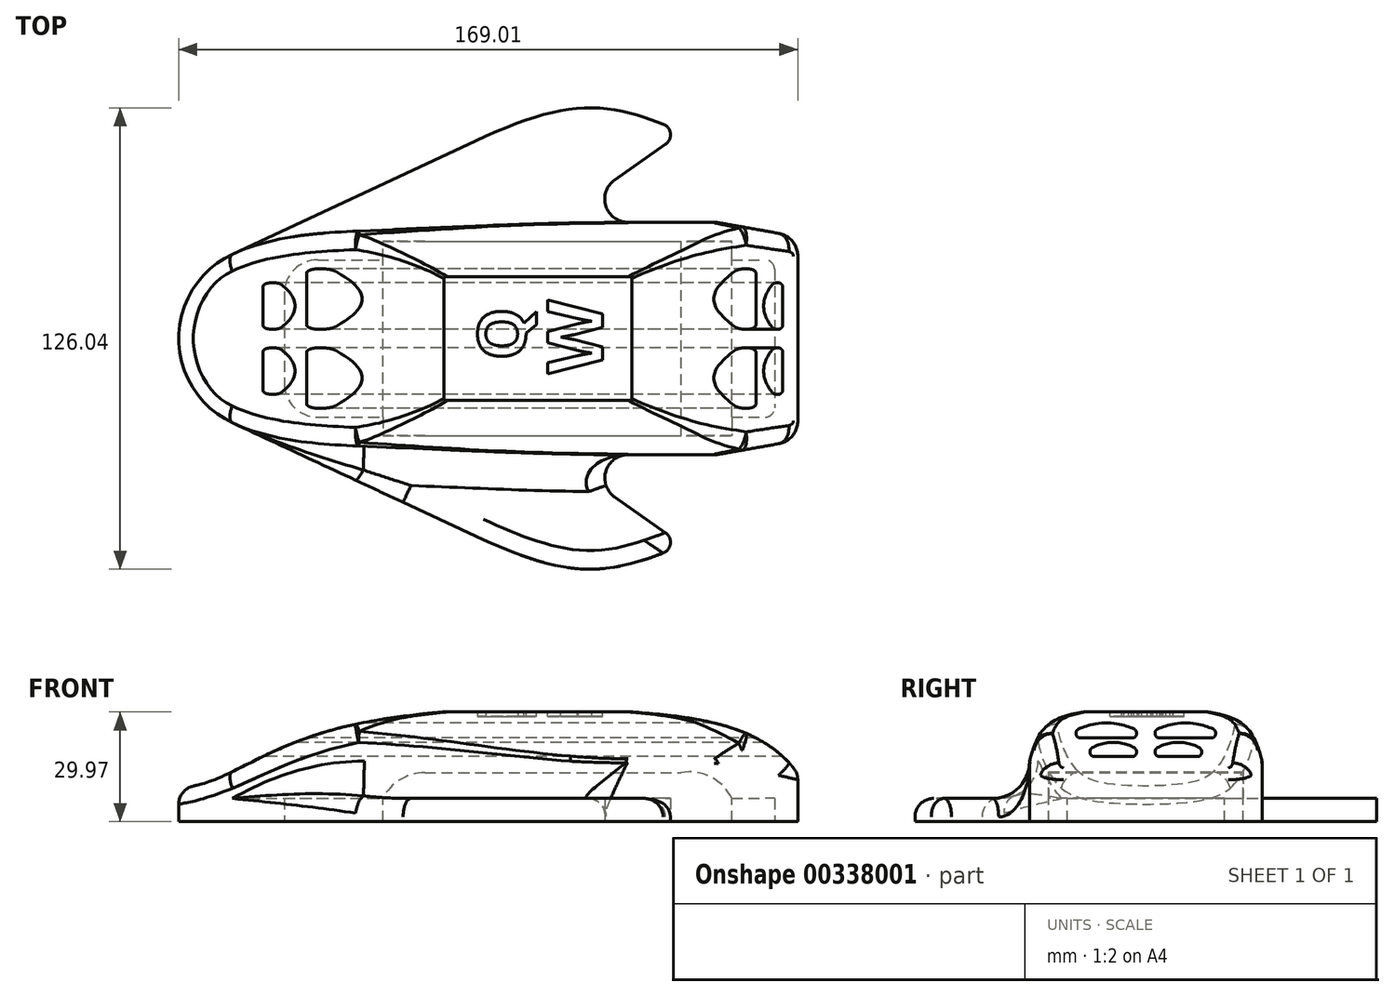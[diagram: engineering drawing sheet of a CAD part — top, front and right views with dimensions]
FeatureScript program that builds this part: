
annotation { "Feature Type Name" : "Feature", "Feature Type Description" : "" }
export const myFeature = defineFeature(function(context is Context, id is Id, definition is map)
    precondition{}
    {
        {
            var Q0;
            Q0=qCreatedBy(makeId("Top.planeOp"),FACE);
            var sketch = newSketch(context, id + "F0", { "sketchPlane" : qUnion([Q0])});
            skLineSegment(sketch, "E0", {"start": v(-59.71, 0) * mm, "end": v(137.74, 0) * mm, "construction": true});
            skLineSegment(sketch, "E1", {"start": v(0, 0) * mm, "end": v(0, 12.32) * mm});
            skLineSegment(sketch, "E2", {"start": v(9.14, 21.46) * mm, "end": v(131.32, 21.46) * mm});
            skLineSegment(sketch, "E3", {"start": v(133.86, 18.92) * mm, "end": v(133.86, 0) * mm});
            skPoint(sketch, "E4.visualSharp", {"position": v(0, 21.46) * mm});
            skArc(sketch, "E4.filletArc", {"start": v(9.14, 21.46) * mm, "mid": v(2.68, 18.78) * mm, "end": v(0, 12.32) * mm});
            skPoint(sketch, "E5.visualSharp", {"position": v(133.86, 21.46) * mm});
            skArc(sketch, "E5.filletArc", {"start": v(133.86, 18.92) * mm, "mid": v(133.11, 20.72) * mm, "end": v(131.32, 21.46) * mm});
            skLineSegment(sketch, "E6", {"start": v(-14.13, 23.02) * mm, "end": v(52.25, 53.98) * mm});
            skLineSegment(sketch, "E7", {"start": v(104.12, 53.03) * mm, "end": v(90.22, 43.3) * mm});
            skLineSegment(sketch, "E8", {"start": v(93.86, 31.75) * mm, "end": v(117.43, 31.75) * mm});
            skLineSegment(sketch, "E9", {"start": v(140.2, 22.5) * mm, "end": v(140.2, 0) * mm});
            skPoint(sketch, "E10.visualSharp", {"position": v(73.72, 31.75) * mm});
            skArc(sketch, "E10.filletArc", {"start": v(90.22, 43.3) * mm, "mid": v(87.8, 36.2) * mm, "end": v(93.86, 31.75) * mm});
            skLineSegment(sketch, "E11", {"start": v(118.53, 31.65) * mm, "end": v(134.96, 28.76) * mm});
            skPoint(sketch, "E12.visualSharp", {"position": v(117.98, 31.75) * mm});
            skArc(sketch, "E12.filletArc", {"start": v(118.53, 31.65) * mm, "mid": v(117.98, 31.73) * mm, "end": v(117.43, 31.75) * mm});
            skPoint(sketch, "E13.visualSharp", {"position": v(140.2, 27.83) * mm});
            skArc(sketch, "E13.filletArc", {"start": v(140.2, 22.5) * mm, "mid": v(138.72, 26.58) * mm, "end": v(134.96, 28.76) * mm});
            skArc(sketch, "E14.MirrorCS", {"start": v(118.53, -31.65) * mm, "mid": v(117.98, -31.73) * mm, "end": v(117.43, -31.75) * mm});
            skArc(sketch, "E15.MirrorCS", {"start": v(133.86, -18.92) * mm, "mid": v(133.11, -20.72) * mm, "end": v(131.32, -21.46) * mm});
            skArc(sketch, "E16.MirrorCS", {"start": v(140.2, -22.5) * mm, "mid": v(138.72, -26.58) * mm, "end": v(134.96, -28.76) * mm});
            skPoint(sketch, "E17.MirrorP", {"position": v(140.2, -27.83) * mm});
            skPoint(sketch, "E18.MirrorP", {"position": v(73.72, -31.75) * mm});
            skPoint(sketch, "E19.MirrorP", {"position": v(117.98, -31.75) * mm});
            skLineSegment(sketch, "E20.MirrorCS", {"start": v(0, 0) * mm, "end": v(0, -12.32) * mm});
            skLineSegment(sketch, "E21.MirrorCS", {"start": v(140.2, -22.5) * mm, "end": v(140.2, 0) * mm});
            skLineSegment(sketch, "E22.MirrorCS", {"start": v(133.86, -18.92) * mm, "end": v(133.86, 0) * mm});
            skPoint(sketch, "E23.MirrorP", {"position": v(0, -21.46) * mm});
            skPoint(sketch, "E24.MirrorP", {"position": v(133.86, -21.46) * mm});
            skLineSegment(sketch, "E25.MirrorCS", {"start": v(118.53, -31.65) * mm, "end": v(134.96, -28.76) * mm});
            skLineSegment(sketch, "E26.MirrorCS", {"start": v(9.14, -21.46) * mm, "end": v(131.32, -21.46) * mm});
            skArc(sketch, "E27.MirrorCS", {"start": v(9.14, -21.46) * mm, "mid": v(2.68, -18.78) * mm, "end": v(0, -12.32) * mm});
            skPoint(sketch, "E28.visualSharp", {"position": v(-63.5, 0) * mm});
            skArc(sketch, "E28.filletArc", {"start": v(-14.13, 23.02) * mm, "mid": v(-24.82, 13.65) * mm, "end": v(-28.8, 0) * mm});
            skFitSpline(sketch, "E29", {"points": [v(106.45, 57.34) * mm, v(86.26, 62.92) * mm, v(52.25, 53.98) * mm], "startDerivative": vector(-36.27, 15.72) * mm, "endDerivative": vector(-75.5, -35.21) * mm});
            skArc(sketch, "E30.filletArc", {"start": v(104.12, 53.03) * mm, "mid": v(105.45, 56) * mm, "end": v(103.47, 58.58) * mm});
            skFitSpline(sketch, "E31.MirrorCS", {"points": [v(106.45, -57.34) * mm, v(86.26, -62.92) * mm, v(52.25, -53.98) * mm], "startDerivative": vector(-36.27, -15.72) * mm, "endDerivative": vector(-75.5, 35.21) * mm});
            skLineSegment(sketch, "E32.MirrorCS", {"start": v(104.12, -53.03) * mm, "end": v(90.22, -43.3) * mm});
            skArc(sketch, "E33.MirrorCS", {"start": v(90.22, -43.3) * mm, "mid": v(87.8, -36.2) * mm, "end": v(93.86, -31.75) * mm});
            skArc(sketch, "E34.MirrorCS", {"start": v(104.12, -53.03) * mm, "mid": v(105.45, -56) * mm, "end": v(103.47, -58.58) * mm});
            skLineSegment(sketch, "E35.MirrorCS", {"start": v(93.86, -31.75) * mm, "end": v(117.43, -31.75) * mm});
            skLineSegment(sketch, "E36.MirrorCS", {"start": v(-14.13, -23.02) * mm, "end": v(52.25, -53.98) * mm});
            skArc(sketch, "E37.MirrorCS", {"start": v(-14.13, -23.02) * mm, "mid": v(-24.82, -13.65) * mm, "end": v(-28.8, 0) * mm});
            skSolve(sketch);
        }
        {
            var Q0;
            Q0 = qSketchRegion(id + "F0", true);
            extrude(context, id + "F1", {"entities" : qUnion([Q0]), "depth" : 6.35 * mm});
        }
        {
            var Q0;
            Q0=makeQuery(id+"F1.opExtrude","CAP_FACE",FACE,{"disambiguationData":[OSD([sQuery(id+"F0.wireOp",EDGE,"E1"),sQuery(id+"F0.wireOp",EDGE,"E2"),sQuery(id+"F0.wireOp",EDGE,"E3"),sQuery(id+"F0.wireOp",EDGE,"E4.filletArc"),sQuery(id+"F0.wireOp",EDGE,"E5.filletArc"),sQuery(id+"F0.wireOp",EDGE,"E6"),sQuery(id+"F0.wireOp",EDGE,"E7"),sQuery(id+"F0.wireOp",EDGE,"E8"),sQuery(id+"F0.wireOp",EDGE,"E9"),sQuery(id+"F0.wireOp",EDGE,"E10.filletArc"),sQuery(id+"F0.wireOp",EDGE,"E11"),sQuery(id+"F0.wireOp",EDGE,"E12.filletArc"),sQuery(id+"F0.wireOp",EDGE,"E13.filletArc"),sQuery(id+"F0.wireOp",EDGE,"E14.MirrorCS"),sQuery(id+"F0.wireOp",EDGE,"E15.MirrorCS"),sQuery(id+"F0.wireOp",EDGE,"E16.MirrorCS"),sQuery(id+"F0.wireOp",EDGE,"E20.MirrorCS"),sQuery(id+"F0.wireOp",EDGE,"E21.MirrorCS"),sQuery(id+"F0.wireOp",EDGE,"E22.MirrorCS"),sQuery(id+"F0.wireOp",EDGE,"E25.MirrorCS"),sQuery(id+"F0.wireOp",EDGE,"E26.MirrorCS"),sQuery(id+"F0.wireOp",EDGE,"E27.MirrorCS"),sQuery(id+"F0.wireOp",EDGE,"E28.filletArc"),sQuery(id+"F0.wireOp",EDGE,"E29"),sQuery(id+"F0.wireOp",EDGE,"E30.filletArc"),sQuery(id+"F0.wireOp",EDGE,"E31.MirrorCS"),sQuery(id+"F0.wireOp",EDGE,"E32.MirrorCS"),sQuery(id+"F0.wireOp",EDGE,"E33.MirrorCS"),sQuery(id+"F0.wireOp",EDGE,"E34.MirrorCS"),sQuery(id+"F0.wireOp",EDGE,"E35.MirrorCS"),sQuery(id+"F0.wireOp",EDGE,"E36.MirrorCS"),sQuery(id+"F0.wireOp",EDGE,"E37.MirrorCS")])],"isStart":false});
            var sketch = newSketch(context, id + "F2", { "sketchPlane" : qUnion([Q0])});
            skLineSegment(sketch, "E38.bottom", {"start": v(99.31, 21.46) * mm, "end": v(122.17, 21.46) * mm});
            skLineSegment(sketch, "E38.top", {"start": v(99.31, 26.54) * mm, "end": v(122.17, 26.54) * mm});
            skLineSegment(sketch, "E38.left", {"start": v(99.31, 21.46) * mm, "end": v(99.31, 26.54) * mm});
            skLineSegment(sketch, "E38.right", {"start": v(122.17, 21.46) * mm, "end": v(122.17, 26.54) * mm});
            skLineSegment(sketch, "E39", {"start": v(0, 0) * mm, "end": v(133.86, 0) * mm, "construction": true});
            skLineSegment(sketch, "E40.MirrorCS", {"start": v(122.17, -21.46) * mm, "end": v(122.17, -26.54) * mm});
            skLineSegment(sketch, "E41.MirrorCS", {"start": v(99.31, -21.46) * mm, "end": v(99.31, -26.54) * mm});
            skLineSegment(sketch, "E42.MirrorCS", {"start": v(99.31, -21.46) * mm, "end": v(122.17, -21.46) * mm});
            skLineSegment(sketch, "E43.MirrorCS", {"start": v(99.31, -26.54) * mm, "end": v(122.17, -26.54) * mm});
            skLineSegment(sketch, "E44.bottom", {"start": v(26.92, 21.46) * mm, "end": v(49.78, 21.46) * mm});
            skLineSegment(sketch, "E44.top", {"start": v(26.92, 26.54) * mm, "end": v(49.78, 26.54) * mm});
            skLineSegment(sketch, "E44.left", {"start": v(26.92, 21.46) * mm, "end": v(26.92, 26.54) * mm});
            skLineSegment(sketch, "E44.right", {"start": v(49.78, 21.46) * mm, "end": v(49.78, 26.54) * mm});
            skLineSegment(sketch, "E45.MirrorCS", {"start": v(26.92, -26.54) * mm, "end": v(49.78, -26.54) * mm});
            skLineSegment(sketch, "E46.MirrorCS", {"start": v(26.92, -21.46) * mm, "end": v(49.78, -21.46) * mm});
            skLineSegment(sketch, "E47.MirrorCS", {"start": v(49.78, -21.46) * mm, "end": v(49.78, -26.54) * mm});
            skLineSegment(sketch, "E48.MirrorCS", {"start": v(26.92, -21.46) * mm, "end": v(26.92, -26.54) * mm});
            skSolve(sketch);
        }
        {
            var Q0;
            Q0 = qSketchRegion(id + "F2", true);
            extrude(context, id + "F3", {"entities" : qUnion([Q0]), "operationType" : NewBodyOperationType.REMOVE, "endBound" : BoundingType.THROUGH_ALL, "oppositeDirection" : true, "depth" : 25.4 * mm});
        }
        {
            var Q0;
            Q0=makeQuery(id+"F1.opExtrude","CAP_FACE",FACE,{"disambiguationData":[OSD([sQuery(id+"F0.wireOp",EDGE,"E1"),sQuery(id+"F0.wireOp",EDGE,"E2"),sQuery(id+"F0.wireOp",EDGE,"E3"),sQuery(id+"F0.wireOp",EDGE,"E4.filletArc"),sQuery(id+"F0.wireOp",EDGE,"E5.filletArc"),sQuery(id+"F0.wireOp",EDGE,"E6"),sQuery(id+"F0.wireOp",EDGE,"E7"),sQuery(id+"F0.wireOp",EDGE,"E8"),sQuery(id+"F0.wireOp",EDGE,"E9"),sQuery(id+"F0.wireOp",EDGE,"E10.filletArc"),sQuery(id+"F0.wireOp",EDGE,"E11"),sQuery(id+"F0.wireOp",EDGE,"E12.filletArc"),sQuery(id+"F0.wireOp",EDGE,"E13.filletArc"),sQuery(id+"F0.wireOp",EDGE,"E14.MirrorCS"),sQuery(id+"F0.wireOp",EDGE,"E15.MirrorCS"),sQuery(id+"F0.wireOp",EDGE,"E16.MirrorCS"),sQuery(id+"F0.wireOp",EDGE,"E20.MirrorCS"),sQuery(id+"F0.wireOp",EDGE,"E21.MirrorCS"),sQuery(id+"F0.wireOp",EDGE,"E22.MirrorCS"),sQuery(id+"F0.wireOp",EDGE,"E25.MirrorCS"),sQuery(id+"F0.wireOp",EDGE,"E26.MirrorCS"),sQuery(id+"F0.wireOp",EDGE,"E27.MirrorCS"),sQuery(id+"F0.wireOp",EDGE,"E28.filletArc"),sQuery(id+"F0.wireOp",EDGE,"E29"),sQuery(id+"F0.wireOp",EDGE,"E30.filletArc"),sQuery(id+"F0.wireOp",EDGE,"E31.MirrorCS"),sQuery(id+"F0.wireOp",EDGE,"E32.MirrorCS"),sQuery(id+"F0.wireOp",EDGE,"E33.MirrorCS"),sQuery(id+"F0.wireOp",EDGE,"E34.MirrorCS"),sQuery(id+"F0.wireOp",EDGE,"E35.MirrorCS"),sQuery(id+"F0.wireOp",EDGE,"E36.MirrorCS"),sQuery(id+"F0.wireOp",EDGE,"E37.MirrorCS")])],"isStart":false});
            var sketch = newSketch(context, id + "F4", { "sketchPlane" : qUnion([Q0])});
            skLineSegment(sketch, "E49.0", {"start": v(93.86, 31.75) * mm, "end": v(117.43, 31.75) * mm});
            skLineSegment(sketch, "E50.0", {"start": v(93.86, -31.75) * mm, "end": v(117.43, -31.75) * mm});
            skArc(sketch, "E51.0", {"start": v(-14.13, 23.02) * mm, "mid": v(-28.8, 0) * mm, "end": v(-14.13, -23.02) * mm});
            skFitSpline(sketch, "E52", {"points": [v(-14.13, -23.02) * mm, v(27.68, -29.68) * mm, v(93.86, -31.75) * mm], "startDerivative": vector(81.8, -38.14) * mm, "endDerivative": vector(126.05, 0) * mm});
            skLineSegment(sketch, "E53.0", {"start": v(118.53, -31.65) * mm, "end": v(134.96, -28.76) * mm});
            skArc(sketch, "E54.0", {"start": v(140.2, -22.5) * mm, "mid": v(138.72, -26.58) * mm, "end": v(134.96, -28.76) * mm});
            skLineSegment(sketch, "E55.0", {"start": v(140.2, -22.5) * mm, "end": v(140.2, 22.5) * mm});
            skPoint(sketch, "E56.0", {"position": v(138.72, 26.58) * mm});
            skArc(sketch, "E57.0", {"start": v(140.2, 22.5) * mm, "mid": v(138.72, 26.58) * mm, "end": v(134.96, 28.76) * mm});
            skLineSegment(sketch, "E58.0", {"start": v(118.53, 31.65) * mm, "end": v(134.96, 28.76) * mm});
            skArc(sketch, "E59.0", {"start": v(118.53, 31.65) * mm, "mid": v(117.98, 31.73) * mm, "end": v(117.43, 31.75) * mm});
            skArc(sketch, "E60.0", {"start": v(118.53, -31.65) * mm, "mid": v(117.98, -31.73) * mm, "end": v(117.43, -31.75) * mm});
            skLineSegment(sketch, "E61", {"start": v(-36.22, 0) * mm, "end": v(156.3, 0) * mm, "construction": true});
            skPoint(sketch, "E61.endSnap0", {"position": v(133.86, 0) * mm});
            skFitSpline(sketch, "E62.MirrorCS", {"points": [v(-14.13, 23.02) * mm, v(27.68, 29.68) * mm, v(93.86, 31.75) * mm], "startDerivative": vector(81.8, 38.14) * mm, "endDerivative": vector(126.05, 0) * mm});
            skSolve(sketch);
        }
        {
            var Q0;
            Q0 = qSketchRegion(id + "F4", true);
            extrude(context, id + "F5", {"entities" : qUnion([Q0]), "operationType" : NewBodyOperationType.ADD, "depth" : 25.4 * mm});
        }
        {
            var Q0;
            Q0=qCreatedBy(makeId("Front.planeOp"),FACE);
            var sketch = newSketch(context, id + "F6", { "sketchPlane" : qUnion([Q0])});
            skFitSpline(sketch, "E63", {"points": [v(-34.74, 3.67) * mm, v(-21.98, 10.44) * mm, v(10.7, 24.38) * mm, v(96.52, 29.85) * mm, v(142.12, 10.31) * mm, v(144.33, 8.88) * mm], "startDerivative": vector(76.62, 125.54) * mm, "endDerivative": vector(-72.53, 307.03) * mm});
            skLineSegment(sketch, "E64", {"start": v(-34.74, 3.67) * mm, "end": v(-35.8, 38.7) * mm});
            skLineSegment(sketch, "E65", {"start": v(-35.8, 38.7) * mm, "end": v(149.91, 37.4) * mm});
            skLineSegment(sketch, "E66", {"start": v(149.91, 37.4) * mm, "end": v(144.33, 8.88) * mm});
            skSolve(sketch);
        }
        {
            var Q0;
            Q0 = qSketchRegion(id + "F6", true);
            extrude(context, id + "F7", {"entities" : qUnion([Q0]), "operationType" : NewBodyOperationType.REMOVE, "endBound" : BoundingType.THROUGH_ALL, "oppositeDirection" : true, "depth" : 25.4 * mm, "hasSecondDirection" : true, "secondDirectionBound" : SecondDirectionBoundingType.THROUGH_ALL, "secondDirectionOppositeDirection" : false, "secondDirectionDepth" : 25.4 * mm});
        }
        {
            var Q0;
            Q0=qCreatedBy(makeId("Right.planeOp"),FACE);
            var sketch = newSketch(context, id + "F8", { "sketchPlane" : qUnion([Q0])});
            skLineSegment(sketch, "E67", {"start": v(0, 35.48) * mm, "end": v(0, -4.46) * mm, "construction": true});
            skFitSpline(sketch, "E68", {"points": [v(-32.03, 15.47) * mm, v(-26.07, 26.9) * mm, v(0, 30.75) * mm], "startDerivative": vector(8.35, 32.15) * mm, "endDerivative": vector(53.08, 0.27) * mm});
            skLineSegment(sketch, "E69", {"start": v(0, 30.75) * mm, "end": v(0, 38.5) * mm});
            skLineSegment(sketch, "E70", {"start": v(0, 38.5) * mm, "end": v(-36.93, 37.2) * mm});
            skLineSegment(sketch, "E71", {"start": v(-36.93, 37.2) * mm, "end": v(-32.03, 15.47) * mm});
            skLineSegment(sketch, "E72.MirrorCS", {"start": v(0, 38.5) * mm, "end": v(36.93, 37.2) * mm});
            skLineSegment(sketch, "E73.MirrorCS", {"start": v(36.93, 37.2) * mm, "end": v(32.03, 15.47) * mm});
            skFitSpline(sketch, "E74.MirrorCS", {"points": [v(32.03, 15.47) * mm, v(26.07, 26.9) * mm, v(0, 30.75) * mm], "startDerivative": vector(-8.35, 32.15) * mm, "endDerivative": vector(-53.08, 0.27) * mm});
            skSolve(sketch);
        }
        {
            var Q0;
            Q0 = qSketchRegion(id + "F8", true);
            extrude(context, id + "F9", {"entities" : qUnion([Q0]), "operationType" : NewBodyOperationType.REMOVE, "endBound" : BoundingType.THROUGH_ALL, "oppositeDirection" : true, "depth" : 25.4 * mm, "hasSecondDirection" : true, "secondDirectionBound" : SecondDirectionBoundingType.THROUGH_ALL, "secondDirectionOppositeDirection" : false, "secondDirectionDepth" : 25.4 * mm});
        }
        {
            var Q0;
            Q0=qCreatedBy(makeId("Right.planeOp"),FACE);
            var sketch = newSketch(context, id + "F10", { "sketchPlane" : qUnion([Q0])});
            skLineSegment(sketch, "E75", {"start": v(0, 0) * mm, "end": v(0, 52.2) * mm, "construction": true});
            skLineSegment(sketch, "E76.top", {"start": v(14.1, 17.78) * mm, "end": v(3.68, 17.78) * mm});
            skLineSegment(sketch, "E76.left", {"start": v(15.24, 19.18) * mm, "end": v(15.24, 18.92) * mm});
            skLineSegment(sketch, "E76.right", {"start": v(2.54, 19.18) * mm, "end": v(2.54, 18.92) * mm});
            skLineSegment(sketch, "E77.top", {"start": v(17.9, 22.86) * mm, "end": v(3.68, 22.86) * mm});
            skLineSegment(sketch, "E77.left", {"start": v(19.05, 24.26) * mm, "end": v(19.05, 24) * mm});
            skLineSegment(sketch, "E77.right", {"start": v(2.54, 24.26) * mm, "end": v(2.54, 24) * mm});
            skPoint(sketch, "E78.visualSharp", {"position": v(19.05, 25.4) * mm});
            skArc(sketch, "E78.filletArc", {"start": v(19.05, 24.26) * mm, "mid": v(18.87, 24.87) * mm, "end": v(18.4, 25.3) * mm});
            skPoint(sketch, "E79.visualSharp", {"position": v(19.05, 22.86) * mm});
            skArc(sketch, "E79.filletArc", {"start": v(17.9, 22.86) * mm, "mid": v(18.72, 23.2) * mm, "end": v(19.05, 24) * mm});
            skPoint(sketch, "E80.visualSharp", {"position": v(2.54, 22.86) * mm});
            skArc(sketch, "E80.filletArc", {"start": v(2.54, 24) * mm, "mid": v(2.87, 23.2) * mm, "end": v(3.68, 22.86) * mm});
            skPoint(sketch, "E81.visualSharp", {"position": v(2.54, 25.4) * mm});
            skArc(sketch, "E81.filletArc", {"start": v(3.2, 25.3) * mm, "mid": v(2.72, 24.87) * mm, "end": v(2.54, 24.26) * mm});
            skPoint(sketch, "E82.visualSharp", {"position": v(2.54, 20.32) * mm});
            skArc(sketch, "E82.filletArc", {"start": v(3.12, 20.17) * mm, "mid": v(2.7, 19.76) * mm, "end": v(2.54, 19.18) * mm});
            skPoint(sketch, "E83.visualSharp", {"position": v(2.54, 17.78) * mm});
            skArc(sketch, "E83.filletArc", {"start": v(2.54, 18.92) * mm, "mid": v(2.87, 18.11) * mm, "end": v(3.68, 17.78) * mm});
            skPoint(sketch, "E84.visualSharp", {"position": v(15.24, 17.78) * mm});
            skArc(sketch, "E84.filletArc", {"start": v(14.1, 17.78) * mm, "mid": v(14.9, 18.11) * mm, "end": v(15.24, 18.92) * mm});
            skPoint(sketch, "E85.visualSharp", {"position": v(15.24, 20.32) * mm});
            skArc(sketch, "E85.filletArc", {"start": v(15.24, 19.18) * mm, "mid": v(15.08, 19.76) * mm, "end": v(14.66, 20.17) * mm});
            skArc(sketch, "E86", {"start": v(18.4, 25.3) * mm, "mid": v(10.8, 26.98) * mm, "end": v(3.2, 25.3) * mm});
            skArc(sketch, "E87", {"start": v(14.66, 20.17) * mm, "mid": v(8.9, 21.68) * mm, "end": v(3.12, 20.17) * mm});
            skLineSegment(sketch, "E88.MirrorCS", {"start": v(-15.24, 19.18) * mm, "end": v(-15.24, 18.92) * mm});
            skLineSegment(sketch, "E89.MirrorCS", {"start": v(-2.54, 19.18) * mm, "end": v(-2.54, 18.92) * mm});
            skLineSegment(sketch, "E90.MirrorCS", {"start": v(-19.05, 24.26) * mm, "end": v(-19.05, 24) * mm});
            skLineSegment(sketch, "E91.MirrorCS", {"start": v(-2.54, 24.26) * mm, "end": v(-2.54, 24) * mm});
            skArc(sketch, "E92.MirrorCS", {"start": v(-3.2, 25.3) * mm, "mid": v(-2.72, 24.87) * mm, "end": v(-2.54, 24.26) * mm});
            skArc(sketch, "E93.MirrorCS", {"start": v(-15.24, 19.18) * mm, "mid": v(-15.08, 19.76) * mm, "end": v(-14.66, 20.17) * mm});
            skArc(sketch, "E94.MirrorCS", {"start": v(-2.54, 18.92) * mm, "mid": v(-2.87, 18.11) * mm, "end": v(-3.68, 17.78) * mm});
            skArc(sketch, "E95.MirrorCS", {"start": v(-3.12, 20.17) * mm, "mid": v(-2.7, 19.76) * mm, "end": v(-2.54, 19.18) * mm});
            skArc(sketch, "E96.MirrorCS", {"start": v(-19.05, 24.26) * mm, "mid": v(-18.87, 24.87) * mm, "end": v(-18.4, 25.3) * mm});
            skArc(sketch, "E97.MirrorCS", {"start": v(-14.1, 17.78) * mm, "mid": v(-14.9, 18.11) * mm, "end": v(-15.24, 18.92) * mm});
            skArc(sketch, "E98.MirrorCS", {"start": v(-17.9, 22.86) * mm, "mid": v(-18.72, 23.2) * mm, "end": v(-19.05, 24) * mm});
            skArc(sketch, "E99.MirrorCS", {"start": v(-2.54, 24) * mm, "mid": v(-2.87, 23.2) * mm, "end": v(-3.68, 22.86) * mm});
            skPoint(sketch, "E100.MirrorP", {"position": v(-19.05, 25.4) * mm});
            skPoint(sketch, "E101.MirrorP", {"position": v(-15.24, 20.32) * mm});
            skPoint(sketch, "E102.MirrorP", {"position": v(-2.54, 17.78) * mm});
            skPoint(sketch, "E103.MirrorP", {"position": v(-2.54, 20.32) * mm});
            skPoint(sketch, "E104.MirrorP", {"position": v(-15.24, 17.78) * mm});
            skPoint(sketch, "E105.MirrorP", {"position": v(-2.54, 22.86) * mm});
            skPoint(sketch, "E106.MirrorP", {"position": v(-19.05, 22.86) * mm});
            skPoint(sketch, "E107.MirrorP", {"position": v(-2.54, 25.4) * mm});
            skArc(sketch, "E108.MirrorCS", {"start": v(-18.4, 25.3) * mm, "mid": v(-10.8, 26.98) * mm, "end": v(-3.2, 25.3) * mm});
            skLineSegment(sketch, "E109.MirrorCS", {"start": v(-14.1, 17.78) * mm, "end": v(-3.68, 17.78) * mm});
            skArc(sketch, "E110.MirrorCS", {"start": v(-14.66, 20.17) * mm, "mid": v(-8.9, 21.68) * mm, "end": v(-3.12, 20.17) * mm});
            skLineSegment(sketch, "E111.MirrorCS", {"start": v(-17.9, 22.86) * mm, "end": v(-3.68, 22.86) * mm});
            skSolve(sketch);
        }
        {
            var Q0;
            Q0 = qSketchRegion(id + "F10", true);
            extrude(context, id + "F11", {"entities" : qUnion([Q0]), "operationType" : NewBodyOperationType.REMOVE, "endBound" : BoundingType.THROUGH_ALL, "depth" : 25.4 * mm, "hasSecondDirection" : true, "secondDirectionBound" : SecondDirectionBoundingType.THROUGH_ALL, "secondDirectionOppositeDirection" : true, "secondDirectionDepth" : 25.4 * mm});
        }
        {
            var Q0;
            Q0=makeQuery(id+"F5.opExtrude","CAP_EDGE",EDGE,{"disambiguationData":[OSD([sQuery(id+"F4.wireOp",EDGE,"E52")])],"isStart":true});
            var Q1;
            Q1=makeQuery(id+"F5.opExtrude","CAP_EDGE",EDGE,{"disambiguationData":[OSD([sQuery(id+"F4.wireOp",EDGE,"E62.MirrorCS")])],"isStart":true});
            fillet(context, id + "F12", {"entities" : qUnion([Q0, Q1]), "radius" : 10.16 * mm, "tangentPropagation" : true, "allowEdgeOverflow" : false});
        }
        {
            var Q0;
            Q0=makeQuery(id+"F7.boolean.opBoolean","INTERSECT",EDGE,{"derivedFrom":[makeQuery(id+"F5.opExtrude","SWEPT_FACE",FACE,{"disambiguationData":[OSD([sQuery(id+"F4.wireOp",EDGE,"E62.MirrorCS")])]}),makeQuery(id+"F7.opExtrude","SWEPT_FACE",FACE,{"disambiguationData":[OSD([sQuery(id+"F6.wireOp",EDGE,"E63")])]})]});
            var Q1;
            Q1=makeQuery(id+"F9.boolean.opBoolean","INTERSECT",EDGE,{"disambiguationData":[OD(0.0)],"derivedFrom":[makeQuery(id+"F7.boolean.opBoolean","COPY",FACE,{"derivedFrom":makeQuery(id+"F7.opExtrude","SWEPT_FACE",FACE,{"disambiguationData":[OSD([sQuery(id+"F6.wireOp",EDGE,"E63")])]})}),makeQuery(id+"F9.opExtrude","SWEPT_FACE",FACE,{"disambiguationData":[OSD([sQuery(id+"F8.wireOp",EDGE,"E68")])]})]});
            var Q2;
            Q2=makeQuery(id+"F9.boolean.opBoolean","INTERSECT",EDGE,{"disambiguationData":[OD(0.0)],"derivedFrom":[makeQuery(id+"F7.boolean.opBoolean","COPY",FACE,{"derivedFrom":makeQuery(id+"F7.opExtrude","SWEPT_FACE",FACE,{"disambiguationData":[OSD([sQuery(id+"F6.wireOp",EDGE,"E63")])]})}),makeQuery(id+"F9.opExtrude","SWEPT_FACE",FACE,{"disambiguationData":[OSD([sQuery(id+"F8.wireOp",EDGE,"E74.MirrorCS")])]})]});
            var Q3;
            Q3=makeQuery(id+"F9.boolean.opBoolean","INTERSECT",EDGE,{"derivedFrom":[makeQuery(id+"F5.opExtrude","SWEPT_FACE",FACE,{"disambiguationData":[OSD([sQuery(id+"F4.wireOp",EDGE,"E52")])]}),makeQuery(id+"F9.opExtrude","SWEPT_FACE",FACE,{"disambiguationData":[OSD([sQuery(id+"F8.wireOp",EDGE,"E68")])]})]});
            var Q4;
            Q4=makeQuery(id+"F9.boolean.opBoolean","INTERSECT",EDGE,{"derivedFrom":[makeQuery(id+"F5.opExtrude","SWEPT_FACE",FACE,{"disambiguationData":[OSD([sQuery(id+"F4.wireOp",EDGE,"E62.MirrorCS")])]}),makeQuery(id+"F9.opExtrude","SWEPT_FACE",FACE,{"disambiguationData":[OSD([sQuery(id+"F8.wireOp",EDGE,"E74.MirrorCS")])]})]});
            var Q5;
            Q5=makeQuery(id+"F9.boolean.opBoolean","INTERSECT",EDGE,{"disambiguationData":[OD(1.0)],"derivedFrom":[makeQuery(id+"F7.boolean.opBoolean","COPY",FACE,{"derivedFrom":makeQuery(id+"F7.opExtrude","SWEPT_FACE",FACE,{"disambiguationData":[OSD([sQuery(id+"F6.wireOp",EDGE,"E63")])]})}),makeQuery(id+"F9.opExtrude","SWEPT_FACE",FACE,{"disambiguationData":[OSD([sQuery(id+"F8.wireOp",EDGE,"E68")])]})]});
            var Q6;
            Q6=makeQuery(id+"F9.boolean.opBoolean","INTERSECT",EDGE,{"disambiguationData":[OD(1.0)],"derivedFrom":[makeQuery(id+"F7.boolean.opBoolean","COPY",FACE,{"derivedFrom":makeQuery(id+"F7.opExtrude","SWEPT_FACE",FACE,{"disambiguationData":[OSD([sQuery(id+"F6.wireOp",EDGE,"E63")])]})}),makeQuery(id+"F9.opExtrude","SWEPT_FACE",FACE,{"disambiguationData":[OSD([sQuery(id+"F8.wireOp",EDGE,"E74.MirrorCS")])]})]});
            fillet(context, id + "F13", {"entities" : qUnion([Q0, Q1, Q2, Q3, Q4, Q5, Q6]), "radius" : 5.08 * mm, "tangentPropagation" : true, "allowEdgeOverflow" : false});
        }
        {
            var Q0;
            {var subQ0=makeQuery(id+"F1.opExtrude","SWEPT_FACE",FACE,{"disambiguationData":[OSD([sQuery(id+"F0.wireOp",EDGE,"E9"),sQuery(id+"F0.wireOp",EDGE,"E21.MirrorCS")])]});var subQ1=makeQuery(id+"F5.opExtrude","SWEPT_FACE",FACE,{"disambiguationData":[OSD([sQuery(id+"F4.wireOp",EDGE,"E55.0")])]});var subQ2=makeQuery(id+"F7.opExtrude","SWEPT_FACE",FACE,{"disambiguationData":[OSD([sQuery(id+"F6.wireOp",EDGE,"E63")])]});Q0=makeQuery(id+"F11.boolean.opBoolean","SPLIT",EDGE,{"disambiguationData":[TD([makeQuery(id+"F1.opExtrude","SWEPT_FACE",FACE,{"disambiguationData":[OSD([sQuery(id+"F0.wireOp",EDGE,"E16.MirrorCS")])]})])],"derivedFrom":makeQuery(id+"F7.boolean.opBoolean","INTERSECT",EDGE,{"derivedFrom":[makeQuery(id+"F5.boolean.opBoolean","MERGE",FACE,{"derivedFrom":[subQ0,subQ1]}),subQ2]})});}
            var Q1;
            Q1=makeQuery(id+"F12.opFillet","BLEND_EDGE",EDGE,{"blendedFrom":[makeQuery(id+"F5.opExtrude","CAP_EDGE",EDGE,{"disambiguationData":[OSD([sQuery(id+"F4.wireOp",EDGE,"E52")])],"isStart":true}),makeQuery(id+"F1.opExtrude","SWEPT_FACE",FACE,{"disambiguationData":[OSD([sQuery(id+"F0.wireOp",EDGE,"E36.MirrorCS")])]})],"blendedInto":[makeQuery(id+"F1.opExtrude","SWEPT_FACE",FACE,{"disambiguationData":[OSD([sQuery(id+"F0.wireOp",EDGE,"E36.MirrorCS")])]})]});
            var Q2;
            Q2=makeQuery(id+"F12.opFillet","BLEND_EDGE",EDGE,{"blendedFrom":[makeQuery(id+"F5.opExtrude","CAP_EDGE",EDGE,{"disambiguationData":[OSD([sQuery(id+"F4.wireOp",EDGE,"E62.MirrorCS")])],"isStart":true}),makeQuery(id+"F1.opExtrude","SWEPT_FACE",FACE,{"disambiguationData":[OSD([sQuery(id+"F0.wireOp",EDGE,"E6")])]})],"blendedInto":[makeQuery(id+"F1.opExtrude","SWEPT_FACE",FACE,{"disambiguationData":[OSD([sQuery(id+"F0.wireOp",EDGE,"E6")])]})]});
            fillet(context, id + "F14", {"entities" : qUnion([Q0, Q1, Q2]), "radius" : 5.08 * mm, "tangentPropagation" : true, "allowEdgeOverflow" : false});
        }
        {
            var Q0;
            Q0=makeQuery(id+"F3.boolean.opBoolean","COPY",FACE,{"derivedFrom":makeQuery(id+"F3.opExtrude","SWEPT_FACE",FACE,{"disambiguationData":[OSD([sQuery(id+"F2.wireOp",EDGE,"E44.top")])]})});
            var sketch = newSketch(context, id + "F15", { "sketchPlane" : qUnion([Q0])});
            skLineSegment(sketch, "E112.0.0", {"start": v(26.92, 0) * mm, "end": v(49.78, 0) * mm});
            skLineSegment(sketch, "E112.0.1", {"start": v(49.78, 0) * mm, "end": v(49.78, 6.35) * mm});
            skLineSegment(sketch, "E112.0.3", {"start": v(26.92, 6.35) * mm, "end": v(26.92, 0) * mm});
            skArc(sketch, "E113", {"start": v(49.78, 6.35) * mm, "mid": v(38.35, 13.37) * mm, "end": v(26.92, 6.35) * mm});
            skSolve(sketch);
        }
        {
            var Q0;
            Q0 = qSketchRegion(id + "F15", true);
            var Q1;
            Q1=makeQuery(id+"F3.boolean.opBoolean","COPY",FACE,{"derivedFrom":makeQuery(id+"F3.opExtrude","SWEPT_FACE",FACE,{"disambiguationData":[OSD([sQuery(id+"F2.wireOp",EDGE,"E45.MirrorCS")])]})});
            extrude(context, id + "F16", {"entities" : qUnion([Q0]), "operationType" : NewBodyOperationType.REMOVE, "endBound" : BoundingType.UP_TO_SURFACE, "endBoundEntityFace" : qUnion([Q1]), "depth" : 25.4 * mm});
        }
        {
            var Q0;
            Q0=makeQuery(id+"F3.boolean.opBoolean","COPY",FACE,{"derivedFrom":makeQuery(id+"F3.opExtrude","SWEPT_FACE",FACE,{"disambiguationData":[OSD([sQuery(id+"F2.wireOp",EDGE,"E38.top")])]})});
            var sketch = newSketch(context, id + "F17", { "sketchPlane" : qUnion([Q0])});
            skArc(sketch, "E114", {"start": v(122.17, 6.35) * mm, "mid": v(110.74, 13.6) * mm, "end": v(99.31, 6.35) * mm});
            skLineSegment(sketch, "E115", {"start": v(99.31, 6.35) * mm, "end": v(122.17, 6.35) * mm});
            skSolve(sketch);
        }
        {
            var Q0;
            Q0 = qSketchRegion(id + "F17", true);
            var Q1;
            Q1=makeQuery(id+"F3.boolean.opBoolean","COPY",FACE,{"derivedFrom":makeQuery(id+"F3.opExtrude","SWEPT_FACE",FACE,{"disambiguationData":[OSD([sQuery(id+"F2.wireOp",EDGE,"E43.MirrorCS")])]})});
            extrude(context, id + "F18", {"entities" : qUnion([Q0]), "operationType" : NewBodyOperationType.REMOVE, "endBound" : BoundingType.UP_TO_SURFACE, "endBoundEntityFace" : qUnion([Q1]), "depth" : 25.4 * mm});
        }
        {
            var Q0;
            Q0=makeQuery(id+"F16.boolean.opBoolean","MERGE",FACE,{"derivedFrom":[makeQuery(id+"F3.boolean.opBoolean","COPY",FACE,{"derivedFrom":makeQuery(id+"F3.opExtrude","SWEPT_FACE",FACE,{"disambiguationData":[OSD([sQuery(id+"F2.wireOp",EDGE,"E44.top")])]})}),makeQuery(id+"F16.opExtrude","CAP_FACE",FACE,{"disambiguationData":[OSD([sQuery(id+"F15.wireOp",EDGE,"E112.0.0"),sQuery(id+"F15.wireOp",EDGE,"E112.0.1"),sQuery(id+"F15.wireOp",EDGE,"E112.0.3"),sQuery(id+"F15.wireOp",EDGE,"E113")])],"isStart":true})]});
            var sketch = newSketch(context, id + "F19", { "sketchPlane" : qUnion([Q0])});
            skLineSegment(sketch, "E116", {"start": v(38.35, 13.37) * mm, "end": v(111.4, 13.37) * mm});
            skLineSegment(sketch, "E117", {"start": v(111.4, 13.37) * mm, "end": v(122.17, 0) * mm});
            skLineSegment(sketch, "E118", {"start": v(122.17, 0) * mm, "end": v(26.92, 0) * mm});
            skLineSegment(sketch, "E119", {"start": v(26.92, 0) * mm, "end": v(38.35, 13.37) * mm});
            skSolve(sketch);
        }
        {
            var Q0;
            Q0 = qSketchRegion(id + "F19", true);
            var Q1;
            {var subQ0=sQuery(id+"F2.wireOp",EDGE,"E43.MirrorCS");Q1=makeQuery(id+"F18.boolean.opBoolean","MERGE",FACE,{"derivedFrom":[makeQuery(id+"F3.boolean.opBoolean","COPY",FACE,{"derivedFrom":makeQuery(id+"F3.opExtrude","SWEPT_FACE",FACE,{"disambiguationData":[OSD([subQ0])]})}),makeQuery(id+"F18.opExtrude","CAP_FACE",FACE,{"disambiguationData":[OSD([subQ0])],"isStart":false})]});}
            extrude(context, id + "F20", {"entities" : qUnion([Q0]), "operationType" : NewBodyOperationType.REMOVE, "endBound" : BoundingType.UP_TO_SURFACE, "endBoundEntityFace" : qUnion([Q1]), "depth" : 25.4 * mm});
        }
        {
            var Q0;
            Q0=qCreatedBy(makeId("Front.planeOp"),FACE);
            var sketch = newSketch(context, id + "F21", { "sketchPlane" : qUnion([Q0])});
            skLineSegment(sketch, "E120.bottom", {"start": v(33.74, 36.97) * mm, "end": v(103.64, 36.97) * mm});
            skLineSegment(sketch, "E120.top", {"start": v(33.74, 29.97) * mm, "end": v(103.64, 29.97) * mm});
            skLineSegment(sketch, "E120.left", {"start": v(33.74, 36.97) * mm, "end": v(33.74, 29.97) * mm});
            skLineSegment(sketch, "E120.right", {"start": v(103.64, 36.97) * mm, "end": v(103.64, 29.97) * mm});
            skSolve(sketch);
        }
        {
            var Q0;
            Q0 = qSketchRegion(id + "F21", true);
            extrude(context, id + "F22", {"entities" : qUnion([Q0]), "operationType" : NewBodyOperationType.REMOVE, "endBound" : BoundingType.THROUGH_ALL, "oppositeDirection" : true, "depth" : 25.4 * mm, "hasSecondDirection" : true, "secondDirectionBound" : SecondDirectionBoundingType.THROUGH_ALL, "secondDirectionOppositeDirection" : false, "secondDirectionDepth" : 25.4 * mm});
        }
        {
            var Q0;
            Q0=makeQuery(id+"F22.boolean.opBoolean","COPY",FACE,{"derivedFrom":makeQuery(id+"F22.opExtrude","SWEPT_FACE",FACE,{"disambiguationData":[OSD([sQuery(id+"F21.wireOp",EDGE,"E120.top")])]})});
            var sketch = newSketch(context, id + "F23", { "sketchPlane" : qUnion([Q0])});
            skText(sketch, "E121", { "text": "Q", "fontName": "OpenSans-Bold.ttf"});
            skText(sketch, "E122", { "text": "W", "fontName": "OpenSans-Bold.ttf"});
            const initialGuessF23  = {"E121": [0.06585, -0.00591, 0.00134, 1, 0.01299], "E122": [0.08686, -0.0097, 0, 1, 0.01503]};
            skSetInitialGuess(sketch, initialGuessF23);
            skSolve(sketch);
        }
        {
            var Q0;
            Q0 = qSketchRegion(id + "F23", true);
            extrude(context, id + "F24", {"entities" : qUnion([Q0]), "operationType" : NewBodyOperationType.REMOVE, "oppositeDirection" : true, "depth" : 1.27 * mm});
        }
    });
